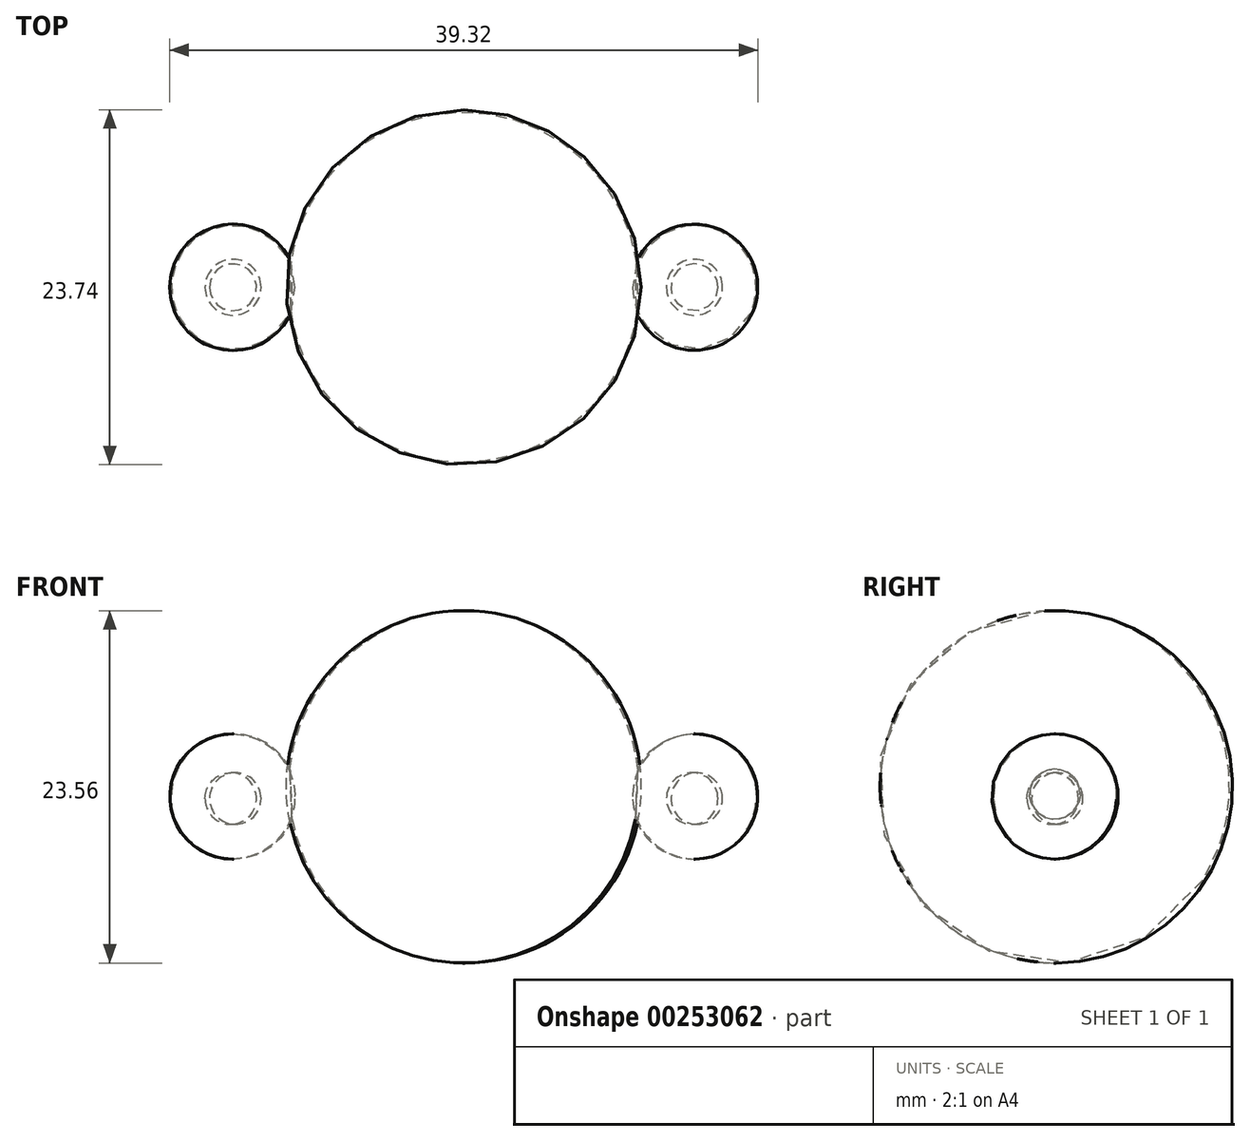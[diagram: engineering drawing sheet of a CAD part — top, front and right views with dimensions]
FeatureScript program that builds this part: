
annotation { "Feature Type Name" : "Feature", "Feature Type Description" : "" }
export const myFeature = defineFeature(function(context is Context, id is Id, definition is map)
    precondition{}
    {
        {
            var Q0;
            Q0=qCreatedBy(makeId("Front.planeOp"),FACE);
            var sketch = newSketch(context, id + "F0", { "sketchPlane" : qUnion([Q0])});
            skLineSegment(sketch, "E0", {"start": v(-7.79, 37.63) * mm, "end": v(-7.79, 14.07) * mm, "construction": true});
            skArc(sketch, "E1", {"start": v(-7.79, 14.07) * mm, "mid": v(3.9, 25.85) * mm, "end": v(-7.79, 37.63) * mm});
            skArc(sketch, "E2", {"start": v(-7.79, 18.46) * mm, "mid": v(0.12, 25.55) * mm, "end": v(-7.79, 32.64) * mm});
            skLineSegment(sketch, "E3", {"start": v(-7.79, 37.63) * mm, "end": v(-7.79, 32.64) * mm});
            skLineSegment(sketch, "E4", {"start": v(-7.79, 18.46) * mm, "end": v(-7.79, 14.07) * mm});
            skLineSegment(sketch, "E5", {"start": v(-7.79, 37.63) * mm, "end": v(-7.79, 14.07) * mm});
            skSolve(sketch);
        }
        {
            var Q0;
            Q0 = qSketchRegion(id + "F0", true);
            var Q1;
            Q1=sQuery(id+"F0.wireOp",EDGE,"E0");
            revolve(context, id + "F1", {"entities" : qUnion([Q0]), "axis" : qUnion([Q1]), "revolveType" : RevolveType.FULL});
        }
        {
            var Q0;
            Q0=qCreatedBy(makeId("Front.planeOp"),FACE);
            var sketch = newSketch(context, id + "F2", { "sketchPlane" : qUnion([Q0])});
            skLineSegment(sketch, "E6", {"start": v(-23.22, 29.38) * mm, "end": v(-23.22, 21.02) * mm, "construction": true});
            skArc(sketch, "E7", {"start": v(-23.22, 29.38) * mm, "mid": v(-27.45, 25.2) * mm, "end": v(-23.22, 21.02) * mm});
            skArc(sketch, "E8", {"start": v(-23.22, 26.78) * mm, "mid": v(-25.1, 25.07) * mm, "end": v(-23.22, 23.35) * mm});
            skLineSegment(sketch, "E9", {"start": v(-23.22, 29.38) * mm, "end": v(-23.22, 26.78) * mm});
            skLineSegment(sketch, "E10", {"start": v(-23.22, 23.35) * mm, "end": v(-23.22, 21.02) * mm});
            skLineSegment(sketch, "E11", {"start": v(-7.78, 37.61) * mm, "end": v(-7.78, 13.97) * mm, "construction": true});
            skSolve(sketch);
        }
        {
            var Q0;
            Q0=makeQuery(id+"F2.imprint","IMPRINT",FACE,{"disambiguationData":[TD([[makeQuery(id+"F2.imprint","IMPRINT",EDGE,{"derivedFrom":sQuery(id+"F2.wireOp",EDGE,"E7")}),1.0]])]});
            var Q1;
            Q1=sQuery(id+"F2.wireOp",EDGE,"E6");
            revolve(context, id + "F3", {"entities" : qUnion([Q0]), "axis" : qUnion([Q1]), "revolveType" : RevolveType.FULL});
        }
        {
            var Q0;
            Q0=qCreatedBy(makeId("Right.planeOp"),FACE);
            cPlane(context, id + "F4", {"entities" : qUnion([Q0]), "cplaneType" : CPlaneType.OFFSET, "offset" : 7.8 * mm, "oppositeDirection" : true, "width" : 150 * mm, "height" : 150 * mm});
        }
        {
            var Q0;
            Q0=makeQuery(id+"F3.opRevolve","SWEPT_BODY",BODY,{"disambiguationData":[OSD([sQuery(id+"F2.wireOp",EDGE,"E7"),sQuery(id+"F2.wireOp",EDGE,"E8"),sQuery(id+"F2.wireOp",EDGE,"E9"),sQuery(id+"F2.wireOp",EDGE,"E10")])]});
            var Q1;
            Q1=qCreatedBy(id+"F4.planeOp",FACE);
            mirror(context, id + "F5", {"operationType" : NewBodyOperationType.ADD, "entities" : qUnion([Q0]), "mirrorPlane" : qUnion([Q1])});
        }
    });
